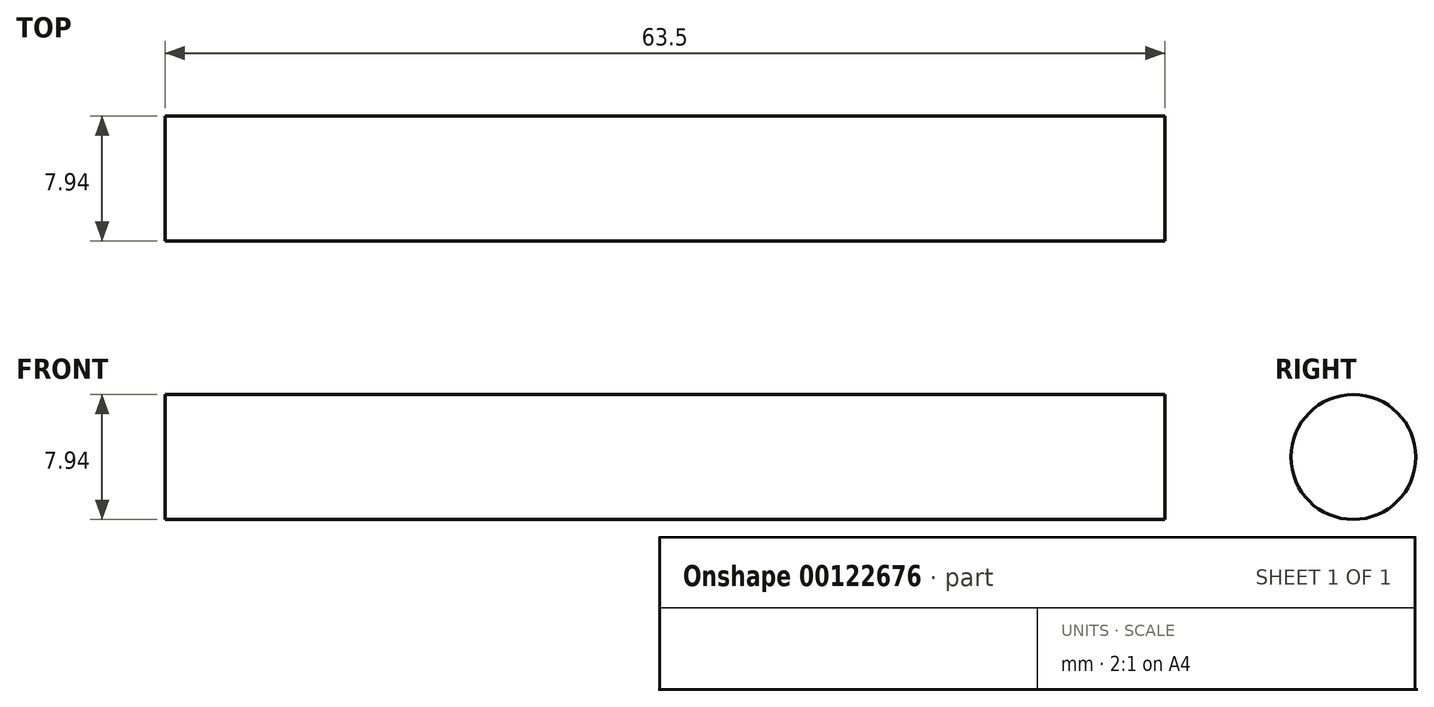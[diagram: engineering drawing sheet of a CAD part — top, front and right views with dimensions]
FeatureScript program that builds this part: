
annotation { "Feature Type Name" : "Feature", "Feature Type Description" : "" }
export const myFeature = defineFeature(function(context is Context, id is Id, definition is map)
    precondition{}
    {
        {
            var Q0;
            Q0=qCreatedBy(makeId("Right.planeOp"),FACE);
            var sketch = newSketch(context, id + "F0", { "sketchPlane" : qUnion([Q0])});
            skCircle(sketch, "E0", {"center": v(0, 0) * mm, "radius": 3.97 * mm});
            skSolve(sketch);
        }
        {
            var Q0;
            Q0=makeQuery(id+"F0.imprint","IMPRINT",FACE,{"disambiguationData":[TD([[makeQuery(id+"F0.imprint","IMPRINT",EDGE,{"derivedFrom":sQuery(id+"F0.wireOp",EDGE,"E0")}),1.0]])]});
            extrude(context, id + "F1", {"entities" : qUnion([Q0]), "depth" : 63.5 * mm});
        }
    });
